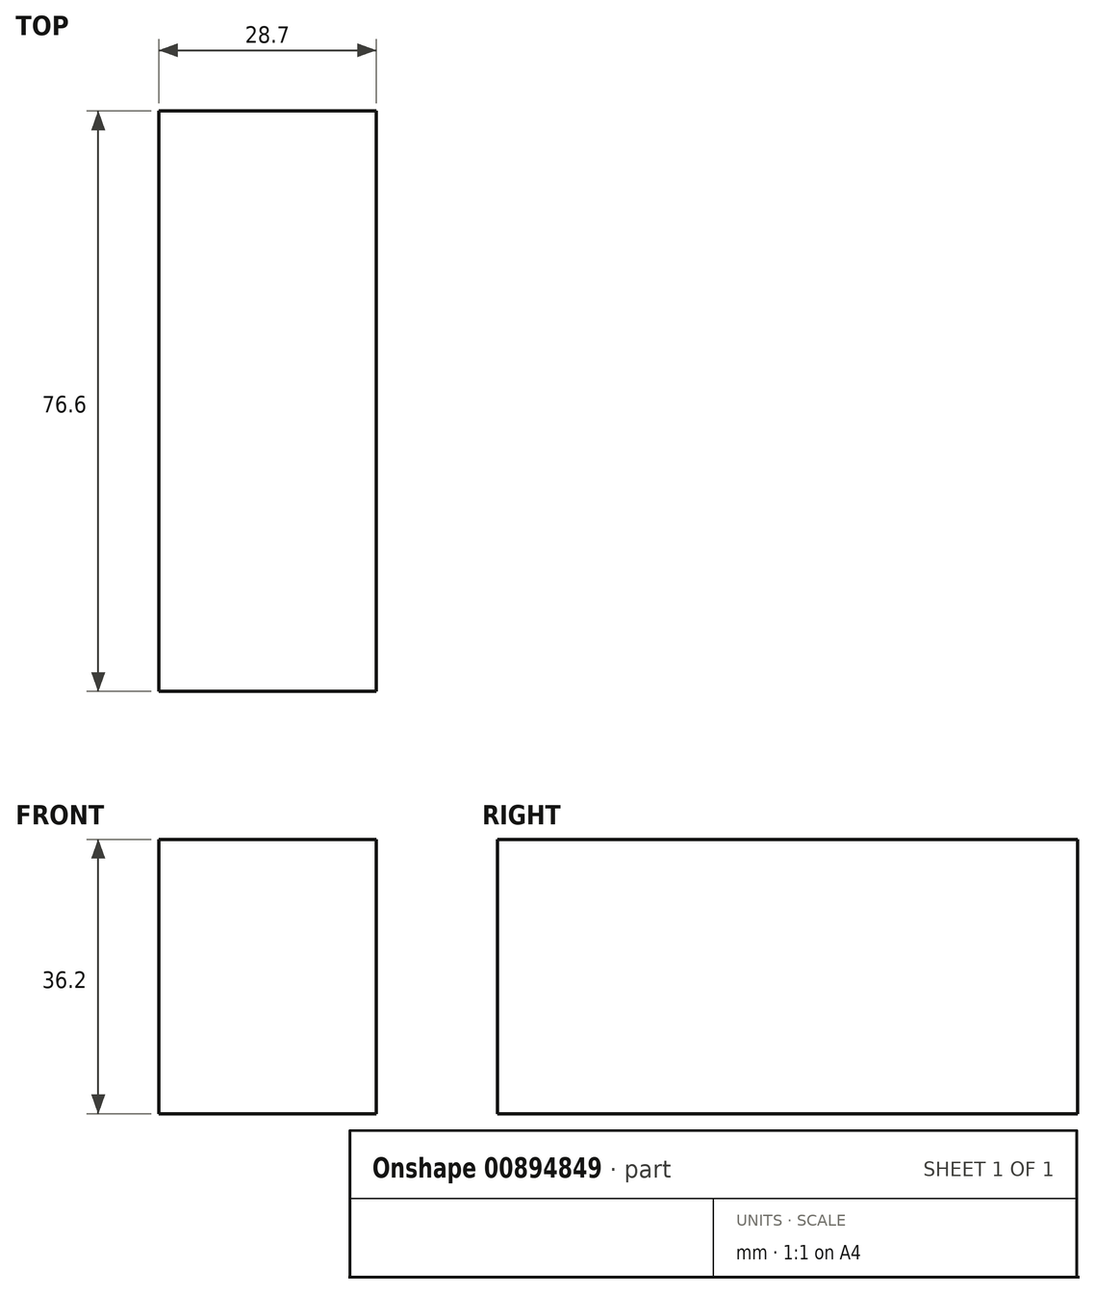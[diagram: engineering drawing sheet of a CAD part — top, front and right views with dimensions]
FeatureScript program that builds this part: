
annotation { "Feature Type Name" : "Feature", "Feature Type Description" : "" }
export const myFeature = defineFeature(function(context is Context, id is Id, definition is map)
    precondition{}
    {
        {
            var Q0;
            Q0=qCreatedBy(makeId("Front.planeOp"),FACE);
            var sketch = newSketch(context, id + "F0", { "sketchPlane" : qUnion([Q0])});
            skLineSegment(sketch, "E0.bottom", {"start": v(0, 0) * mm, "end": v(28.7, 0) * mm});
            skLineSegment(sketch, "E0.top", {"start": v(0, -36.2) * mm, "end": v(28.7, -36.2) * mm});
            skLineSegment(sketch, "E0.left", {"start": v(0, 0) * mm, "end": v(0, -36.2) * mm});
            skLineSegment(sketch, "E0.right", {"start": v(28.7, 0) * mm, "end": v(28.7, -36.2) * mm});
            skSolve(sketch);
        }
        {
            var Q0;
            Q0=makeQuery(id+"F0.imprint","IMPRINT",FACE,{"disambiguationData":[TD([[makeQuery(id+"F0.imprint","IMPRINT",EDGE,{"derivedFrom":sQuery(id+"F0.wireOp",EDGE,"E0.bottom")}),-1.0]])]});
            extrude(context, id + "F1", {"entities" : qUnion([Q0]), "depth" : 76.6 * mm, "offsetDistance" : 25 * mm});
        }
    });
